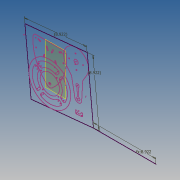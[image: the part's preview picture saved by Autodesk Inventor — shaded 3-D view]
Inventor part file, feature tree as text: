
AUTODESK INVENTOR PART (.ipt)
format: ipt  version: 2013 (Build 170138000, 138)  size: 98,816 bytes
history: native  units: in
note: dims shown in document units (in); Inventor stores cm internally (conversion verified against a paired STEP export)
features: reference x5, plane x1, sketch x1
ambient origin geometry x8: Origin, YZ Plane, XZ Plane, XY Plane, X Axis, Y Axis, Z Axis, Center Point
feature tree (7):
  plane  "Work Plane1"
  sketch  "Sketch1"  dims[d0=8.9218in d1=8.9218in d2=8.9218in]
  reference  "Reference1"
  reference  "Reference2"
  reference  "Reference3"
  reference  "Reference4"
  reference  "Reference5"
